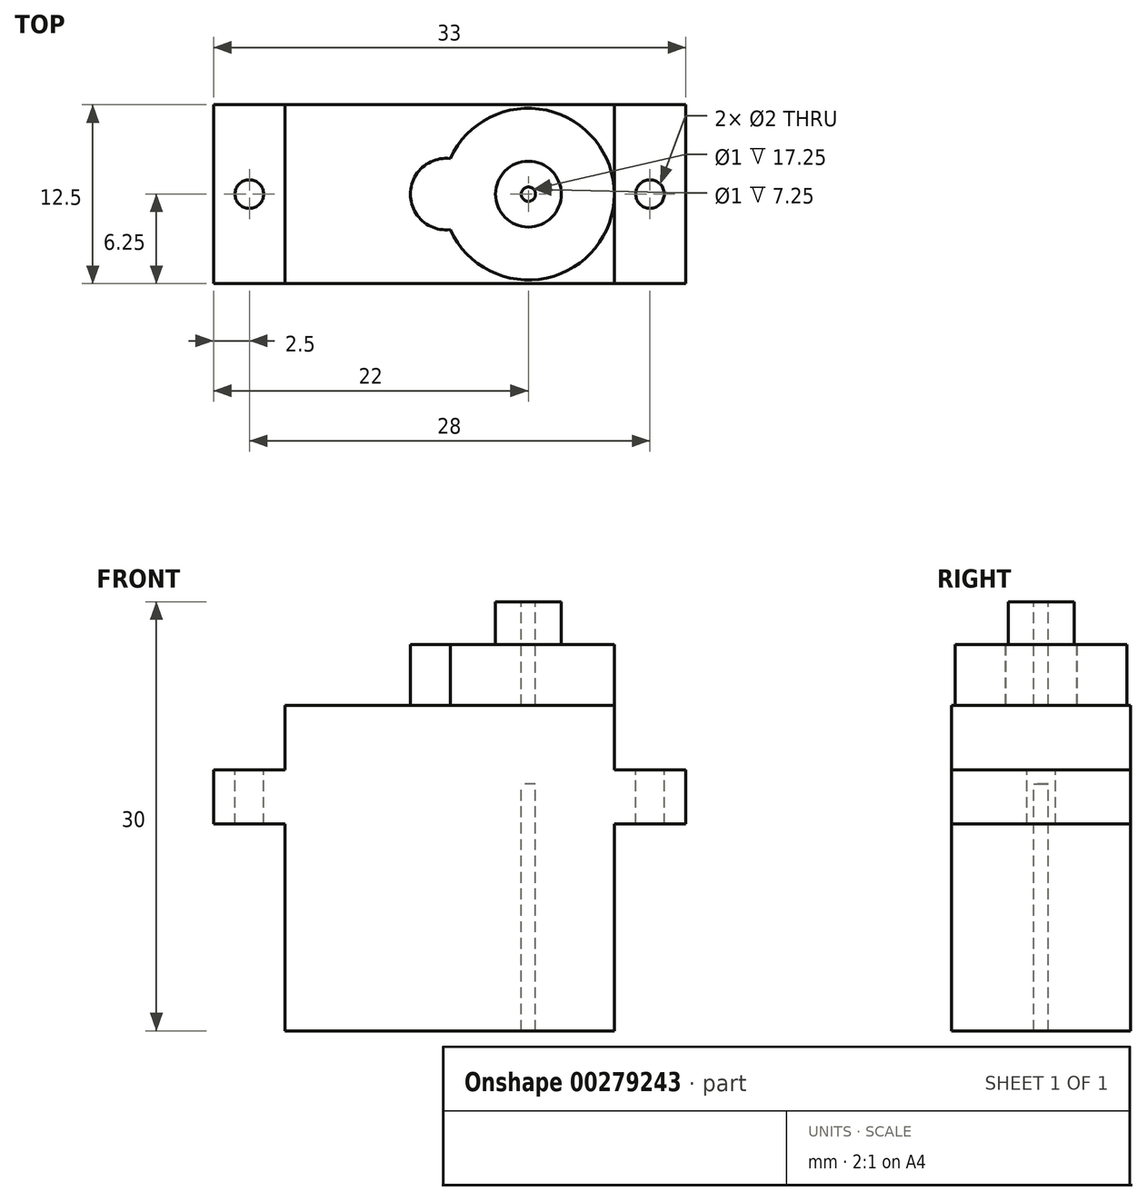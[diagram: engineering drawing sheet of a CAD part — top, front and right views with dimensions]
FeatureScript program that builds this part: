
annotation { "Feature Type Name" : "Feature", "Feature Type Description" : "" }
export const myFeature = defineFeature(function(context is Context, id is Id, definition is map)
    precondition{}
    {
        {
            var Q0;
            Q0=qCreatedBy(makeId("Top.planeOp"),FACE);
            var sketch = newSketch(context, id + "F0", { "sketchPlane" : qUnion([Q0])});
            skLineSegment(sketch, "E0.bottom", {"start": v(11.5, -6.25) * mm, "end": v(-11.5, -6.25) * mm});
            skLineSegment(sketch, "E0.top", {"start": v(11.5, 6.25) * mm, "end": v(-11.5, 6.25) * mm});
            skLineSegment(sketch, "E0.left", {"start": v(11.5, -6.25) * mm, "end": v(11.5, 6.25) * mm});
            skLineSegment(sketch, "E0.right", {"start": v(-11.5, -6.25) * mm, "end": v(-11.5, 6.25) * mm});
            skPoint(sketch, "E0.middle", {"position": v(0, 0) * mm});
            skLineSegment(sketch, "E1.bottom", {"start": v(11.5, 6.25) * mm, "end": v(16.5, 6.25) * mm});
            skLineSegment(sketch, "E1.top", {"start": v(11.5, -6.25) * mm, "end": v(16.5, -6.25) * mm});
            skLineSegment(sketch, "E1.left", {"start": v(11.5, 6.25) * mm, "end": v(11.5, -6.25) * mm});
            skLineSegment(sketch, "E1.right", {"start": v(16.5, 6.25) * mm, "end": v(16.5, -6.25) * mm});
            skCircle(sketch, "E2", {"center": v(14, 0) * mm, "radius": 1 * mm});
            skLineSegment(sketch, "E3.MirrorCS", {"start": v(-11.5, 6.25) * mm, "end": v(-16.5, 6.25) * mm});
            skCircle(sketch, "E4.MirrorC", {"center": v(-14, 0) * mm, "radius": 1 * mm});
            skLineSegment(sketch, "E5.MirrorCS", {"start": v(-16.5, 6.25) * mm, "end": v(-16.5, -6.25) * mm});
            skLineSegment(sketch, "E6.MirrorCS", {"start": v(-11.5, -6.25) * mm, "end": v(-16.5, -6.25) * mm});
            skCircle(sketch, "E7", {"center": v(5.5, 0) * mm, "radius": 6 * mm});
            skCircle(sketch, "E8", {"center": v(-0.25, 0) * mm, "radius": 2.5 * mm});
            skCircle(sketch, "E9", {"center": v(5.5, 0) * mm, "radius": 2.3 * mm});
            skCircle(sketch, "E10", {"center": v(5.5, 0) * mm, "radius": 0.5 * mm});
            skSolve(sketch);
        }
        {
            var Q0;
            {var subQ7=sQuery(id+"F0.wireOp",EDGE,"E0.bottom");Q0=makeQuery(id+"F0.imprint","IMPRINT",FACE,{"disambiguationData":[TD([[makeQuery(id+"F0.imprint","IMPRINT",EDGE,{"derivedFrom":subQ7}),-1.0]])]});}
            var Q1;
            {var subQ0=sQuery(id+"F0.wireOp",EDGE,"E8");var subQ1=sQuery(id+"F0.wireOp",EDGE,"E7");var subQ2=makeQuery(id+"F0.imprint","INTERSECT",VERTEX,{"disambiguationData":[OD(0.0)],"derivedFrom":[subQ1,subQ0]});Q1=makeQuery(id+"F0.imprint","IMPRINT",FACE,{"disambiguationData":[TD([[makeQuery(id+"F0.imprint","IMPRINT",EDGE,{"disambiguationData":[TD([[subQ2,-1.0]])],"derivedFrom":subQ1}),-1.0]])]});}
            var Q2;
            {var subQ0=sQuery(id+"F0.wireOp",EDGE,"E8");var subQ1=sQuery(id+"F0.wireOp",EDGE,"E7");var subQ2=makeQuery(id+"F0.imprint","INTERSECT",VERTEX,{"disambiguationData":[OD(0.0)],"derivedFrom":[subQ1,subQ0]});Q2=makeQuery(id+"F0.imprint","IMPRINT",FACE,{"disambiguationData":[TD([[makeQuery(id+"F0.imprint","IMPRINT",EDGE,{"disambiguationData":[TD([[subQ2,-1.0]])],"derivedFrom":subQ1}),1.0]])]});}
            var Q3;
            Q3=makeQuery(id+"F0.imprint","IMPRINT",FACE,{"disambiguationData":[TD([[makeQuery(id+"F0.imprint","IMPRINT",EDGE,{"derivedFrom":sQuery(id+"F0.wireOp",EDGE,"E9")}),-1.0]])]});
            var Q4;
            Q4=makeQuery(id+"F0.imprint","IMPRINT",FACE,{"disambiguationData":[TD([[makeQuery(id+"F0.imprint","IMPRINT",EDGE,{"derivedFrom":sQuery(id+"F0.wireOp",EDGE,"E9")}),1.0]])]});
            extrude(context, id + "F1", {"entities" : qUnion([Q0, Q1, Q2, Q3, Q4]), "oppositeDirection" : true, "depth" : 22.75 * mm});
        }
        {
            var Q0;
            Q0=makeQuery(id+"F0.imprint","IMPRINT",FACE,{"disambiguationData":[TD([[makeQuery(id+"F0.imprint","IMPRINT",EDGE,{"derivedFrom":sQuery(id+"F0.wireOp",EDGE,"E9")}),1.0]])]});
            var Q1;
            Q1=makeQuery(id+"F0.imprint","IMPRINT",FACE,{"disambiguationData":[TD([[makeQuery(id+"F0.imprint","IMPRINT",EDGE,{"derivedFrom":sQuery(id+"F0.wireOp",EDGE,"E9")}),-1.0]])]});
            var Q2;
            {var subQ0=sQuery(id+"F0.wireOp",EDGE,"E8");var subQ1=sQuery(id+"F0.wireOp",EDGE,"E7");var subQ2=makeQuery(id+"F0.imprint","INTERSECT",VERTEX,{"disambiguationData":[OD(0.0)],"derivedFrom":[subQ1,subQ0]});Q2=makeQuery(id+"F0.imprint","IMPRINT",FACE,{"disambiguationData":[TD([[makeQuery(id+"F0.imprint","IMPRINT",EDGE,{"disambiguationData":[TD([[subQ2,-1.0]])],"derivedFrom":subQ1}),1.0]])]});}
            var Q3;
            {var subQ0=sQuery(id+"F0.wireOp",EDGE,"E8");var subQ1=sQuery(id+"F0.wireOp",EDGE,"E7");var subQ2=makeQuery(id+"F0.imprint","INTERSECT",VERTEX,{"disambiguationData":[OD(0.0)],"derivedFrom":[subQ1,subQ0]});Q3=makeQuery(id+"F0.imprint","IMPRINT",FACE,{"disambiguationData":[TD([[makeQuery(id+"F0.imprint","IMPRINT",EDGE,{"disambiguationData":[TD([[subQ2,-1.0]])],"derivedFrom":subQ1}),-1.0]])]});}
            extrude(context, id + "F2", {"entities" : qUnion([Q0, Q1, Q2, Q3]), "operationType" : NewBodyOperationType.ADD, "depth" : 4.25 * mm});
        }
        {
            var Q0;
            Q0=makeQuery(id+"F0.imprint","IMPRINT",FACE,{"disambiguationData":[TD([[makeQuery(id+"F0.imprint","IMPRINT",EDGE,{"derivedFrom":sQuery(id+"F0.wireOp",EDGE,"E9")}),1.0]])]});
            extrude(context, id + "F3", {"entities" : qUnion([Q0]), "operationType" : NewBodyOperationType.ADD, "depth" : 7.25 * mm});
        }
        {
            var Q0;
            {var subQ3=sQuery(id+"F0.wireOp",EDGE,"E1.bottom");Q0=makeQuery(id+"F0.imprint","IMPRINT",FACE,{"disambiguationData":[TD([[makeQuery(id+"F0.imprint","IMPRINT",EDGE,{"derivedFrom":subQ3}),-1.0]])]});}
            extrude(context, id + "F4", {"entities" : qUnion([Q0]), "operationType" : NewBodyOperationType.ADD, "oppositeDirection" : true, "depth" : 8.3 * mm, "hasSecondDirection" : true, "secondDirectionOppositeDirection" : true, "secondDirectionDepth" : 4.5 * mm});
        }
        {
            var Q0;
            Q0=makeQuery(id+"F0.imprint","IMPRINT",FACE,{"disambiguationData":[TD([[makeQuery(id+"F0.imprint","IMPRINT",EDGE,{"derivedFrom":sQuery(id+"F0.wireOp",EDGE,"E0.right")}),1.0]])]});
            extrude(context, id + "F5", {"entities" : qUnion([Q0]), "operationType" : NewBodyOperationType.ADD, "oppositeDirection" : true, "depth" : 8.3 * mm, "hasSecondDirection" : true, "secondDirectionOppositeDirection" : true, "secondDirectionDepth" : 4.5 * mm});
        }
        {
            var Q0;
            Q0=makeQuery(id+"F0.imprint","IMPRINT",FACE,{"disambiguationData":[TD([[makeQuery(id+"F0.imprint","IMPRINT",EDGE,{"derivedFrom":sQuery(id+"F0.wireOp",EDGE,"E10")}),1.0]])]});
            extrude(context, id + "F6", {"entities" : qUnion([Q0]), "operationType" : NewBodyOperationType.ADD, "oppositeDirection" : true, "depth" : 5.5 * mm});
        }
    });
